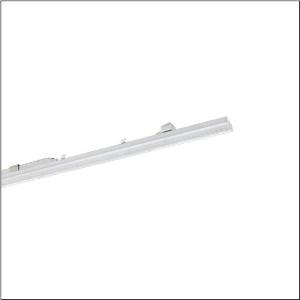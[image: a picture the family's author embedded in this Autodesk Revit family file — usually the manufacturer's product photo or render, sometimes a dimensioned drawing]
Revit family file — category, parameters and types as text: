
# Revit family: tl_l_5wd7a8p0h2b5
name_source: partatom
category: Lighting Fixtures
units: mm (PartAtom-declared; Revit-internal decimal feet)

## family parameters
Cut with Voids When Loaded = No
Host = Face
Light Source = No
Part Type = Normal
Room Calculation Point = No
Round Connector Dimension = Use Diameter
Shared = No

## types (1)
- --- (1 x LED, 5000 lm, 31.5 W, 4000K)
    Apparent Load = 32 VA
    CIE Flux Codes = 49 84 98 100 100
    Color Rendering = 80
    Color Temperature = 4000K
    Default Elevation = 1800 mm
    Description = TL L, luminaire insert, of sheet steel, galvanised, coil coated, white, length: 1.500mm, width: 66mm, height: 67mm, surge protection,LED light colour: 840, control gear: DALI, with terminal, 5-pole, mains connection: 230..240V, AC, 50/60Hz, rated input power: 63W, micro fuse,primary optical cover: cover, of PMMA, light emission: direct distribution, protection rating (complete): as luminaire, insulation class (complete): insulation class I (protective earthing), certification: CE, impact resistance: IK06, permissible ambient temperature for indoor applications: -35..+35°C, standard: NMF01, packaging unit: 1 piece
    Height = 120 mm
    Lamp = 1 x LED
    Lamp Light Flux = 5000 lm
    Lamp Power = 31.5 W
    Lamp count = 1
    Length = 1690 mm
    Luminous efficacy = 159 lm/W
    Manufacturer = Siteco
    ModVariant = No
    Model = 5WD7A8P0H2B5
    Mounting Place = Ceiling
    Mounting Type = Pendant
    Number of Poles = 1
    OnlyDefault = Yes
    Power Factor = 1
    Product Name = TL L
    Product group = luminaire insert
    ProductGroupID = 901
    Protection Class = Protection class I
    Protection Degree = Degree of protection
    RLX_Detail_Level = 1
    RLX_Emergency_Light_Flux = 0 lm
    RLX_Emergency_Type = 0
    RLX_Emergency_Type_DB = No
    RlxData = <blob elided: 17361 chars, md5=2f948187>
    Socket = socket
    Standby Power = 0 W
    System Light Flux = 5000 lm
    System Power = 32 W
    Type Comments = factory setting: luminous flux: 100 % | dim-lin: 254 | 646 mA
    Type Image = l_1294382.jpg
    URL = http://relux.com
    VarID = @adj_000543
    Voltage = 0 V
    Weight = 0.00 kg
    Width = 208 mm

## geometry (parser evidence)
native form markers: Blend x4, Sweep x10
no freeform markers — native parametric forms only
